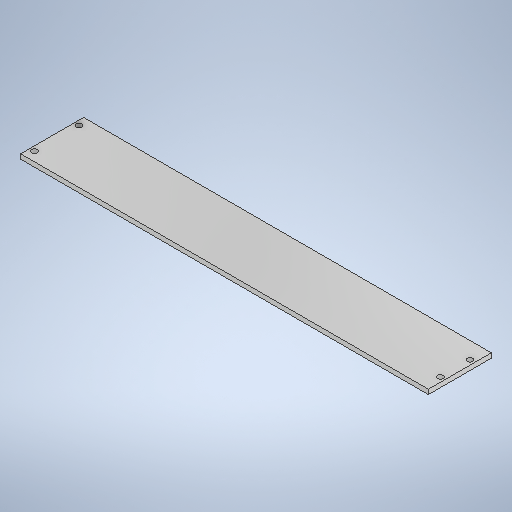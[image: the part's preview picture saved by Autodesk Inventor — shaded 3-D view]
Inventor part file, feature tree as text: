
AUTODESK INVENTOR PART (.ipt)
format: ipt  version: 2025.1 (Build 291241020, 241B)  size: 302,592 bytes
history: native  units: in
note: dims shown in document units (in); Inventor stores cm internally (conversion verified against a paired STEP export)
features: sketch x8, extrude x7, hole x1, projected_geometry x1
ambient origin geometry x8: Origin, YZ Plane, XZ Plane, XY Plane, X Axis, Y Axis, Z Axis, Center Point
bodies: Solid1 (feature_tree)
feature tree (17):
  extrude  "Extrusion1"  Depth=11.0in
  extrude  "Extrusion2"  Depth=1.7in
  extrude  "Extrusion3"  Depth=0.0625in
  extrude  "Extrusion4"  Depth=0.3976in
  extrude  "Extrusion5"  TaperAngle=0.0deg  [1 undecoded]
  extrude  "Extrusion6"  Depth=0.125in
  extrude  "Extrusion7"  Depth=0.6in
  hole  "Hole1"  [1 undecoded]
  sketch  "Sketch1"  dims[d0=11.0in d1=2.5in]
  sketch  "Sketch2"  dims[d2=1.7in d3=0.0in d4=0.0625in]
  sketch  "Sketch3"  dims[d5=0.0625in d6=0.0625in]
  sketch  "Sketch4"  dims[d7=1.5in d8=0.0in d9=0.3976in]
  sketch  "Sketch5"  dims[d10=0.8in d11=0.0in d12=0.0in]
  sketch  "Sketch7"  dims[d13=0.125in d15=0.8in]
  sketch  "Sketch8"  dims[d16=0.4in d17=0.6in]
  projected_geometry  "Projected Loop1"
  sketch  "Sketch9"  dims[d18=0.1875in d19=1.0in d20=0.0in d21=0.125in d22=0.6102in d23=0.6102in d24=1.0in d25=0.0in d26=0.0in d27=0.0in d28=0.125in d29=0.0in d30=0.45in d31=0.125in d32=0.45in d33=0.125in d34=0.125in d35=0.125in d36=0.25in d37=0.25in d38=0.15in d39=0.75in d40=0.5in d41=0.093in d42=0.5635in d43=0.885in d44=0.8108in]
note: 2 required parameter values undecoded (feature->parameter linkage not recoverable at this tier; creation-order binding heuristic only, values carry confidence <= 0.55)
